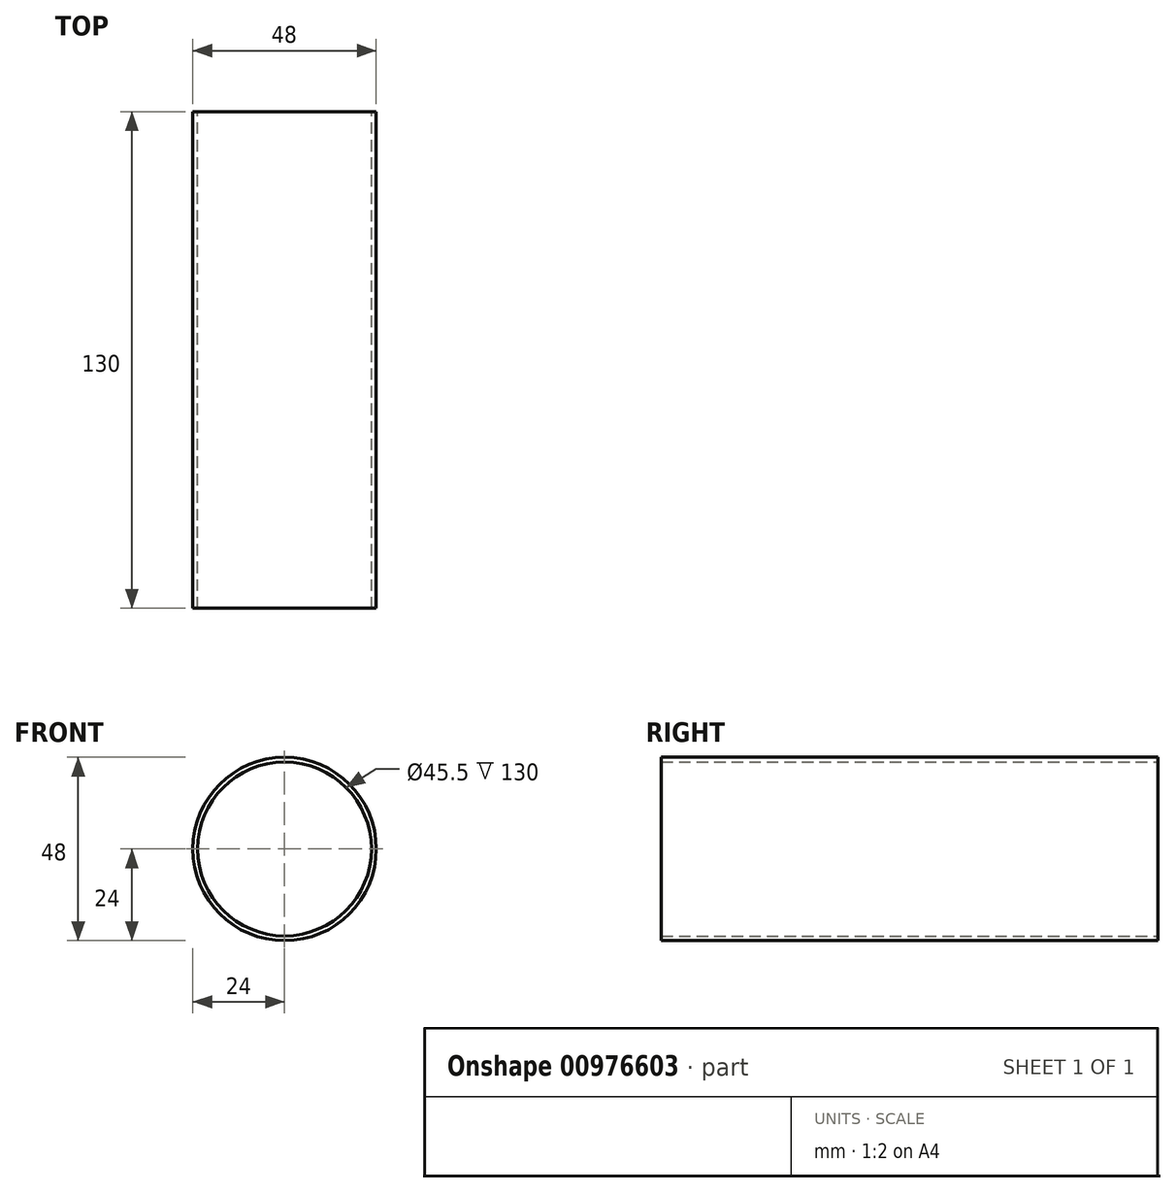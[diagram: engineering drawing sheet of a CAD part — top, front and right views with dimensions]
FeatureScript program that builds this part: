
annotation { "Feature Type Name" : "Feature", "Feature Type Description" : "" }
export const myFeature = defineFeature(function(context is Context, id is Id, definition is map)
    precondition{}
    {
        {
            var Q0;
            Q0=qCreatedBy(makeId("Front.planeOp"),FACE);
            var sketch = newSketch(context, id + "F0", { "sketchPlane" : qUnion([Q0])});
            skCircle(sketch, "E0", {"center": v(0, 0) * mm, "radius": 24 * mm});
            skCircle(sketch, "E1", {"center": v(0, 0) * mm, "radius": 22.75 * mm});
            skSolve(sketch);
        }
        {
            var Q0;
            Q0=makeQuery(id+"F0.imprint","IMPRINT",FACE,{"disambiguationData":[TD([[makeQuery(id+"F0.imprint","IMPRINT",EDGE,{"derivedFrom":sQuery(id+"F0.wireOp",EDGE,"E0")}),1.0]])]});
            extrude(context, id + "F1", {"entities" : qUnion([Q0]), "depth" : 130 * mm, "offsetDistance" : 25 * mm, "symmetric" : true});
        }
    });
